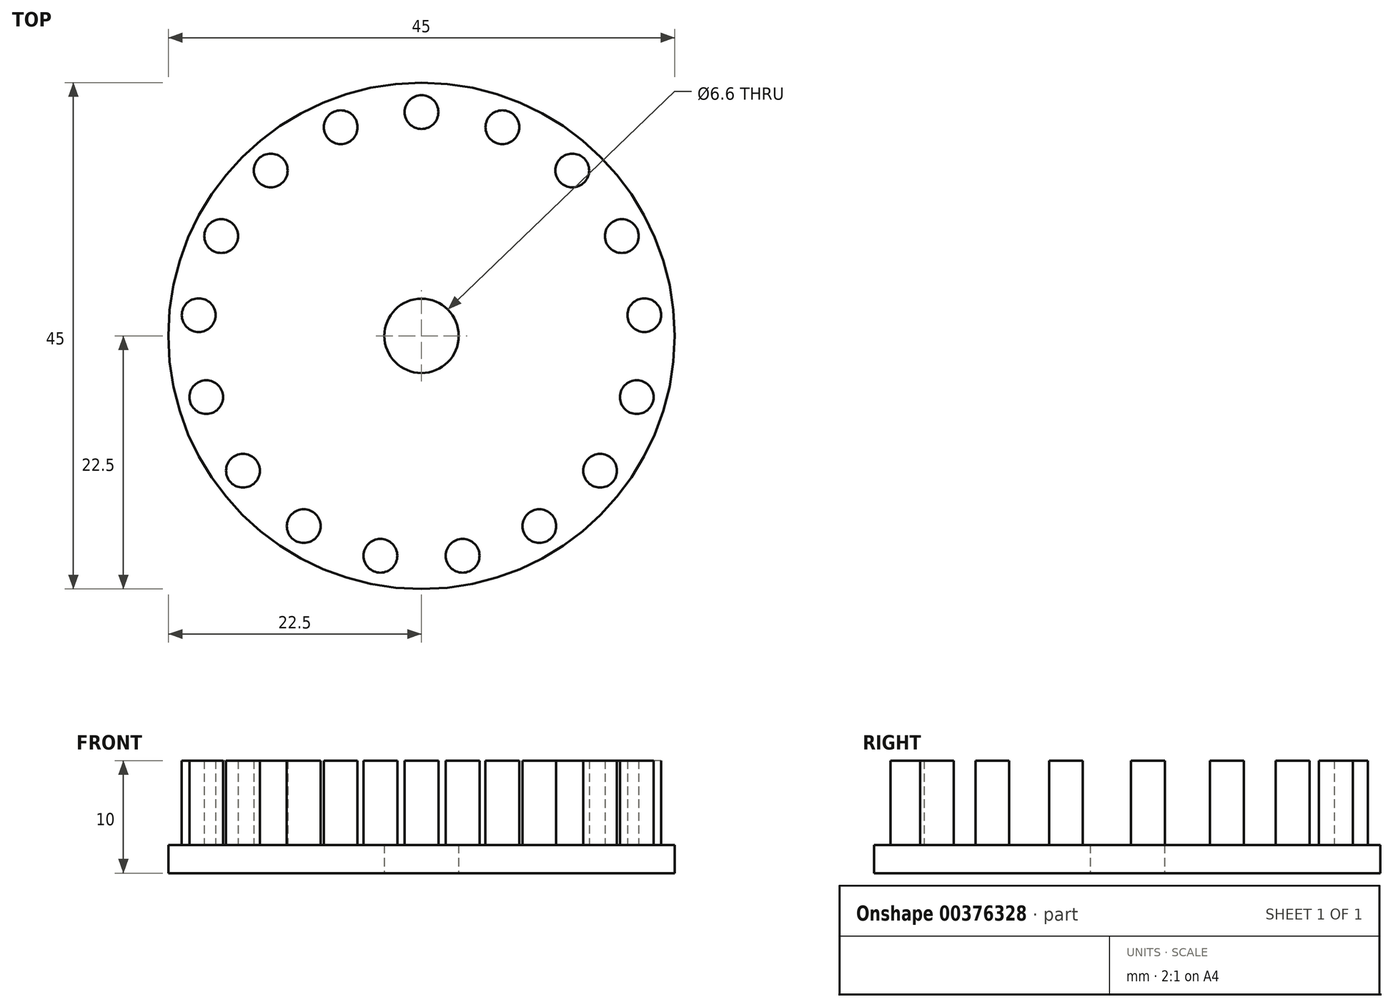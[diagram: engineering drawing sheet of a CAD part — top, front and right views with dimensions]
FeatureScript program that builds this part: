
annotation { "Feature Type Name" : "Feature", "Feature Type Description" : "" }
export const myFeature = defineFeature(function(context is Context, id is Id, definition is map)
    precondition{}
    {
        {
            var Q0;
            Q0=qCreatedBy(makeId("Top.planeOp"),FACE);
            var sketch = newSketch(context, id + "F0", { "sketchPlane" : qUnion([Q0])});
            skCircle(sketch, "E0", {"center": v(0, 0) * mm, "radius": 3.3 * mm});
            skCircle(sketch, "E1", {"center": v(0, 0) * mm, "radius": 22.5 * mm});
            skSolve(sketch);
        }
        {
            var Q0;
            Q0 = qSketchRegion(id + "F0", true);
            extrude(context, id + "F1", {"entities" : qUnion([Q0]), "depth" : 2.5 * mm});
        }
        {
            var Q0;
            Q0=makeQuery(id+"F1.opExtrude","CAP_FACE",FACE,{"disambiguationData":[OSD([sQuery(id+"F0.wireOp",EDGE,"E0"),sQuery(id+"F0.wireOp",EDGE,"E1")])],"isStart":false});
            var sketch = newSketch(context, id + "F2", { "sketchPlane" : qUnion([Q0])});
            skCircle(sketch, "E2", {"center": v(0, 19.89) * mm, "radius": 1.5 * mm});
            skCircle(sketch, "E3.1.0", {"center": v(-7.18, 18.54) * mm, "radius": 1.5 * mm});
            skCircle(sketch, "E3.2.0", {"center": v(-13.4, 14.7) * mm, "radius": 1.5 * mm});
            skCircle(sketch, "E3.3.0", {"center": v(-17.8, 8.86) * mm, "radius": 1.5 * mm});
            skCircle(sketch, "E3.4.0", {"center": v(-19.8, 1.83) * mm, "radius": 1.5 * mm});
            skCircle(sketch, "E3.5.0", {"center": v(-19.13, -5.44) * mm, "radius": 1.5 * mm});
            skCircle(sketch, "E3.6.0", {"center": v(-15.87, -11.98) * mm, "radius": 1.5 * mm});
            skCircle(sketch, "E3.7.0", {"center": v(-10.47, -16.9) * mm, "radius": 1.5 * mm});
            skCircle(sketch, "E3.8.0", {"center": v(-3.65, -19.55) * mm, "radius": 1.5 * mm});
            skCircle(sketch, "E3.9.0", {"center": v(3.65, -19.55) * mm, "radius": 1.5 * mm});
            skCircle(sketch, "E3.10.0", {"center": v(10.47, -16.9) * mm, "radius": 1.5 * mm});
            skCircle(sketch, "E3.11.0", {"center": v(15.87, -11.98) * mm, "radius": 1.5 * mm});
            skCircle(sketch, "E3.12.0", {"center": v(19.13, -5.44) * mm, "radius": 1.5 * mm});
            skCircle(sketch, "E3.13.0", {"center": v(19.8, 1.83) * mm, "radius": 1.5 * mm});
            skCircle(sketch, "E3.14.0", {"center": v(17.8, 8.86) * mm, "radius": 1.5 * mm});
            skCircle(sketch, "E3.15.0", {"center": v(13.4, 14.7) * mm, "radius": 1.5 * mm});
            skCircle(sketch, "E3.16.0", {"center": v(7.18, 18.54) * mm, "radius": 1.5 * mm});
            skPoint(sketch, "E3.center", {"position": v(0, 0) * mm});
            skSolve(sketch);
        }
        {
            var Q0;
            Q0 = qSketchRegion(id + "F2", true);
            extrude(context, id + "F3", {"entities" : qUnion([Q0]), "operationType" : NewBodyOperationType.ADD, "depth" : 7.5 * mm});
        }
    });
